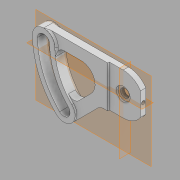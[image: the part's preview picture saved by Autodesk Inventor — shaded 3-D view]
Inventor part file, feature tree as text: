
AUTODESK INVENTOR PART (.ipt)
format: ipt  version: 2020 (Build 240168000, 168)  size: 238,592 bytes
history: native  units: in
note: dims shown in document units (in); Inventor stores cm internally (conversion verified against a paired STEP export)
features: sketch x7, extrude x6, projected_geometry x4, other x1, hole x1, fillet x1
ambient origin geometry x8: Origin, YZ Plane, XZ Plane, XY Plane, X Axis, Y Axis, Z Axis, Center Point
bodies: Body1 (feature_tree)
feature tree (20):
  other  "Sólido1"
  extrude  "Cabezal"  Depth=1.25in
  hole  "Broca y barreno"  [1 undecoded]
  extrude  "Mango"  Depth=0.12in
  extrude  "AgujeroLateral"  Depth=1.62in
  extrude  "BloqueCentral"  Depth=1.62in
  extrude  "HuecoMango"  Depth=0.625in TaperAngle=0.0deg
  extrude  "HuecoCentral"  Depth=0.12in
  fillet  "Empalme1"  Radius=1.6583in
  sketch  "Boceto1"  dims[d0=3.0in d2=1.25in]
  sketch  "Boceto3"  dims[d3=1.0in d4=0.38in d5=0.0in]
  sketch  "Boceto4"  dims[d6=0.625in d7=0.75in d8=1.0in d9=0.12in d10=0.5635in d11=1.0in d12=0.8108in d14=0.69in]
  sketch  "Boceto8"  dims[d15=0.5in d19=1.62in]
  projected_geometry  "Contorno proyectado2"
  sketch  "Boceto9"  dims[d21=135.0deg d22=1.62in]
  projected_geometry  "Contorno proyectado5"
  sketch  "Boceto10"  dims[d25=0.5in d28=0.625in d29=0.0in]
  projected_geometry  "Contorno proyectado6"
  sketch  "Boceto11"  dims[d36=0.25in d37=0.19in d38=1.6583in d39=0.8292in d40=0.38in d41=0.0in d47=45.0deg d48=0.5in d49=0.5in d50=0.0in d52=0.88in d53=0.88in d54=0.0in d55=0.125in d56=0.0in d57=1.0in d58=1.0in d59=2.0in d60=0.81in d61=0.81in d62=0.5in d63=0.0in d64=0.12in]
  projected_geometry  "Contorno proyectado7"
note: 1 required parameter value undecoded (feature->parameter linkage not recoverable at this tier; creation-order binding heuristic only, values carry confidence <= 0.55)
